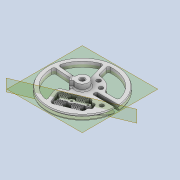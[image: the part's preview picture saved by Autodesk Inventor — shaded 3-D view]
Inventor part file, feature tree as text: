
AUTODESK INVENTOR PART (.ipt)
format: ipt  version: 2020 (Build 240168000, 168)  size: 1,702,912 bytes
history: native  units: mm
features: sketch x21, extrude x20, projected_geometry x18, fillet x15, thicken_offset x9, chamfer x6, other x3, pattern_linear x2, plane x2, revolve x1, mirror x1, reference x1
ambient origin geometry x8: Origin, YZ Plane, XZ Plane, XY Plane, X Axis, Y Axis, Z Axis, Center Point
bodies: Solid1 (feature_tree)
feature tree (99):
  extrude  "Extrusion1"  Depth=3.0mm TaperAngle=0.0deg
  revolve  "Revolution1"  [1 undecoded]
  extrude  "Extrusion2"  Depth=6.0mm
  extrude  "Extrusion3"  Depth=11.0mm
  extrude  "Extrusion4"  Depth=34.0mm
  extrude  "Extrusion5"  Depth=14.0mm
  chamfer  "Chamfer1"  Distance=5.0mm
  fillet  "Fillet1"  Radius=2.5mm
  fillet  "Fillet2"  Radius=15.0mm
  extrude  "Extrusion6"  Depth=0.5mm
  extrude  "Extrusion7"  TaperAngle=45.0deg  [1 undecoded]
  extrude  "Extrusion8"  Depth=12.0mm
  pattern_linear  "Rectangular Pattern1"  Count1=2  [1 undecoded]
  pattern_linear  "Rectangular Pattern2"  Spacing1=3.5mm  [1 undecoded]
  thicken_offset  "Thicken1"
  chamfer  "Chamfer2"  Distance=0.5mm
  plane  "Work Plane1"
  mirror  "Mirror1"
  extrude  "Extrusion9"  Depth=1.0mm TaperAngle=0.0deg
  fillet  "Fillet3"  Radius=40.0mm
  fillet  "Fillet4"  Radius=10.0mm
  fillet  "Fillet5"  Radius=1.0mm
  fillet  "Fillet6"  Radius=1.0mm
  extrude  "Extrusion10"  Depth=1.0mm TaperAngle=45.0deg
  fillet  "Fillet7"  Radius=5.0mm
  chamfer  "Chamfer3"  Distance=4.0mm
  extrude  "Extrusion11"  Depth=1.0mm TaperAngle=0.0deg
  fillet  "Fillet8"  Radius=2.0mm
  thicken_offset  "Thicken2"
  fillet  "Fillet9"  Radius=2.0mm
  extrude  "Extrusion12"  Depth=1.0mm
  thicken_offset  "Thicken3"
  thicken_offset  "Thicken4"
  chamfer  "Chamfer4"  Distance=0.5mm
  plane  "Work Plane2"
  extrude  "Extrusion13"  Depth=1.5mm
  chamfer  "Chamfer5"  Distance=3.0mm
  extrude  "Extrusion14"  Depth=1.0mm
  extrude  "Extrusion15"  Depth=1.0mm TaperAngle=0.0deg
  fillet  "Fillet10"  Radius=0.2mm
  fillet  "Fillet11"  Radius=0.5mm
  fillet  "Fillet12"  Radius=1.5mm
  thicken_offset  "Thicken5"
  thicken_offset  "Thicken6"
  thicken_offset  "Thicken7"
  extrude  "Extrusion16"  Depth=1.0mm
  extrude  "Extrusion17"  Depth=1.0mm
  extrude  "Extrusion18"  Depth=1.0mm TaperAngle=0.0deg
  extrude  "Extrusion19"  Depth=1.0mm
  thicken_offset  "Thicken8"
  thicken_offset  "Thicken9"
  extrude  "Extrusion20"  Depth=1.0mm
  fillet  "Fillet13"  Radius=5.0mm
  fillet  "Fillet14"  Radius=0.5mm
  chamfer  "Chamfer6"  Distance=7.3mm
  fillet  "Fillet15"  Radius=7.330383mm
  sketch  "Sketch1"  dims[d0=50.0mm d1=3.0mm d2=0.0mm]
  sketch  "Sketch2"  dims[d3=1.5mm d4=1.5mm]
  projected_geometry  "Projected Loop1"
  sketch  "Sketch3"  dims[d5=90.0deg d6=6.0mm]
  sketch  "Sketch4"  dims[d7=3.0mm d8=0.0mm d9=11.0mm]
  projected_geometry  "Projected Loop2"
  sketch  "Sketch5"  dims[d10=5.0mm d11=0.0mm d12=34.0mm]
  projected_geometry  "Projected Loop3"
  sketch  "Sketch6"  dims[d13=3.0mm d14=14.0mm d15=5.0mm d16=0.0mm d17=2.5mm d18=15.0mm d19=0.0mm]
  projected_geometry  "Projected Loop4"
  sketch  "Sketch7"  dims[d20=0.5mm d21=2.0mm d22=45.0deg d23=0.5mm]
  projected_geometry  "Projected Loop5"
  sketch  "Sketch8"  dims[d24=1.0mm d25=45.0deg]
  projected_geometry  "Projected Loop6"
  sketch  "Sketch9"  dims[d26=3.0mm d27=12.0mm d28=20.0mm]
  projected_geometry  "Projected Loop7"
  projected_geometry  "Projected Loop8"
  sketch  "Sketch10"  dims[d29=15.0mm d30=0.0mm]
  projected_geometry  "Projected Loop9"
  sketch  "Sketch11"  dims[d31=4.0mm]
  projected_geometry  "Projected Loop10"
  sketch  "Sketch12"  dims[d32=4.0mm]
  projected_geometry  "Projected Loop11"
  sketch  "Sketch13"  dims[d33=2.0mm]
  projected_geometry  "Projected Loop12"
  sketch  "Sketch14"  dims[d34=14.0mm]
  reference  "Reference1"
  sketch  "Sketch15"  dims[d35=3.0mm d36=0.0mm]
  projected_geometry  "Projected Loop13"
  sketch  "Sketch16"  dims[d37=3.0mm]
  projected_geometry  "Projected Loop14"
  sketch  "Sketch17"  dims[d38=0.5mm]
  sketch  "Sketch18"  dims[d39=0.5mm]
  sketch  "Sketch19"  dims[d40=2.2mm]
  projected_geometry  "Projected Loop15"
  projected_geometry  "Projected Loop16"
  sketch  "Sketch20"  dims[d41=3.5mm]
  projected_geometry  "Projected Loop17"
  sketch  "Sketch21"  dims[d42=0.5mm d43=3.5mm d44=0.5mm d45=3.0mm d46=0.0mm d47=40.0mm d49=1.3mm d50=20.0mm d52=10.0mm d53=1.0mm d54=1.0mm d55=1.0mm d56=2.0mm d57=45.0deg d58=5.0mm d59=4.0mm d60=3.0mm d61=0.0mm d62=2.0mm d63=2.0mm d64=1.0mm d65=0.5mm d66=1.5mm d67=3.0mm d68=3.0mm d69=3.0mm d70=0.0mm d71=0.2mm d72=0.5mm d73=2.0mm d74=45.0deg d75=1.5mm d76=1.4mm d77=1.4mm d78=3.0mm d79=0.0mm d80=1.0mm d81=5.0mm d82=5.0mm d83=0.5mm d84=7.3mm d85=7.330383mm d86=3.0mm d87=3.0mm d88=0.0mm d89=0.5mm d90=0.5mm d91=0.5mm d92=0.5mm d93=0.5mm d94=2.0mm d95=45.0deg d96=-2.0mm d97=1.0mm d98=4.5mm d99=0.0mm d100=1.0mm d101=2.0mm d102=45.0deg d103=6.108652mm d104=6.981317mm d105=10.0mm d106=3.1mm d107=10.0mm d108=3.1mm d109=4.5mm d110=0.0mm d111=18.0mm d112=46.0mm d113=2.5mm d114=2.5mm d115=2.5mm d116=2.5mm d117=26.0mm d118=3.0mm d119=4.712389mm d120=12.217305mm d121=4.5mm d122=0.0mm d123=4.0mm d124=1.0mm d125=1.5mm d126=2.0mm d127=2.0mm d128=2.0mm d129=2.0mm d130=1.0mm d131=1.0mm d132=4.5mm d133=0.0mm d134=3.0mm d135=4.5mm d136=0.0mm d137=12.0mm d138=25.481807mm d139=4.0mm d140=4.5mm d141=0.0mm d142=4.5mm d143=0.0mm d144=1.0mm d145=1.0mm d146=1.0mm d147=1.0mm d148=3.3mm d149=1.4mm d150=6.0mm d151=0.0mm d152=1.0mm d153=1.0mm d154=0.5mm d155=2.0mm d156=45.0deg d157=1.0mm]
  projected_geometry  "Projected Loop18"
  parser-record x1  (decoder bookkeeping rows leaked as tree rows — omitted from the tree; the rows remain in map.json)
  other  "driver_ass_1.iam"
  other  "bearing_3_6_2:1"
note: 4 required parameter values undecoded (feature->parameter linkage not recoverable at this tier; creation-order binding heuristic only, values carry confidence <= 0.55)
note: 1 file-system path scrubbed to <path> (originals preserved in map.json)